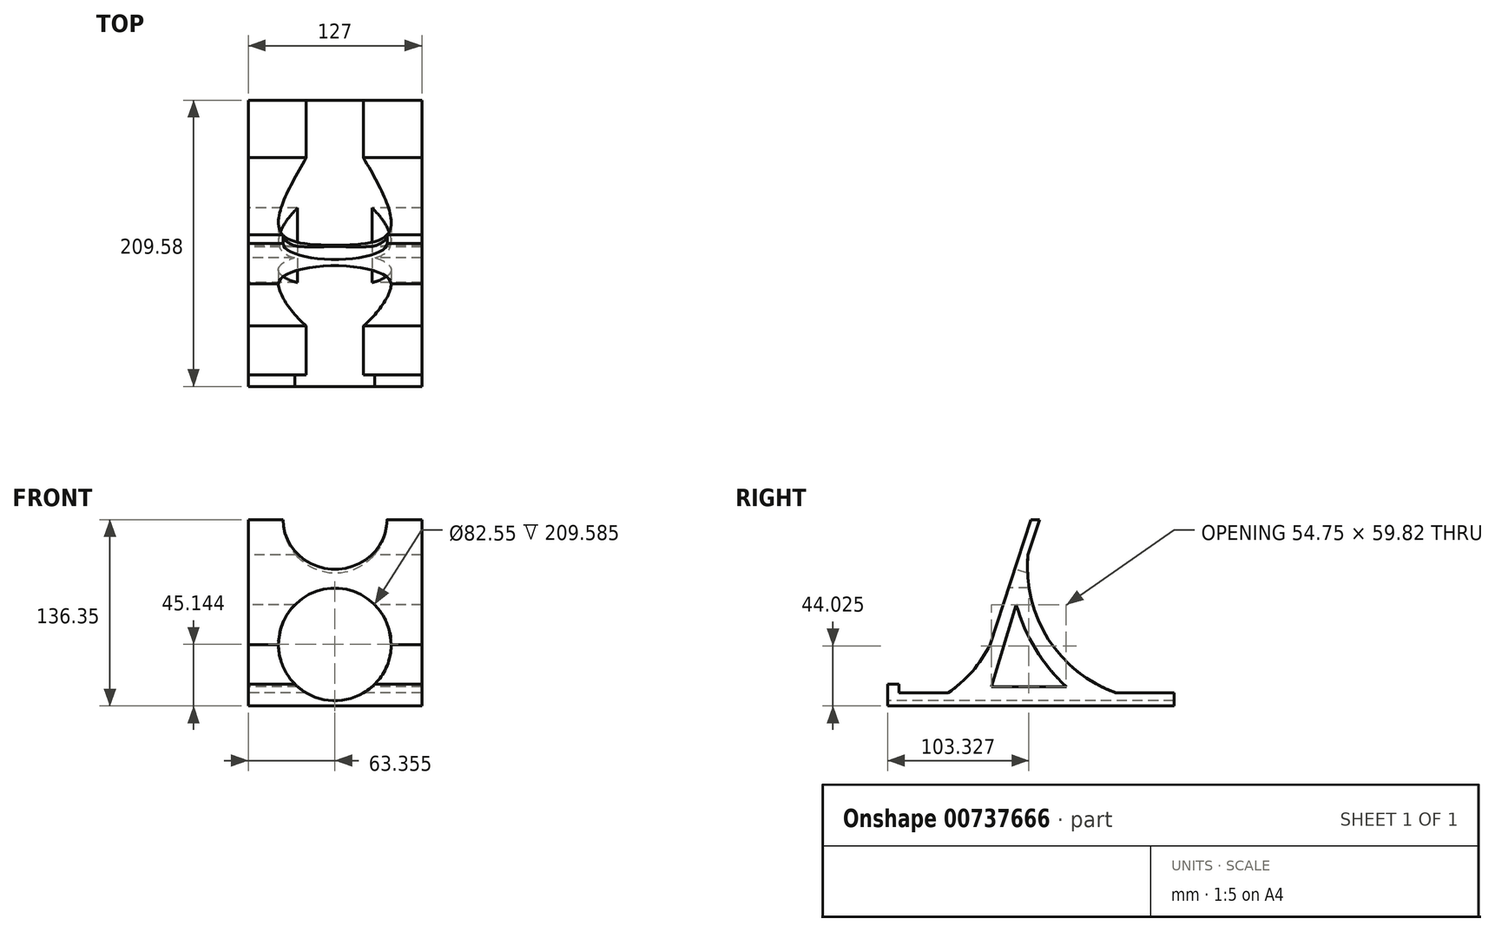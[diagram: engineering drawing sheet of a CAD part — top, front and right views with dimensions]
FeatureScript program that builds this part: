
annotation { "Feature Type Name" : "Feature", "Feature Type Description" : "" }
export const myFeature = defineFeature(function(context is Context, id is Id, definition is map)
    precondition{}
    {
        {
            var Q0;
            Q0=qCreatedBy(makeId("Right.planeOp"),FACE);
            var sketch = newSketch(context, id + "F0", { "sketchPlane" : qUnion([Q0])});
            skLineSegment(sketch, "E0", {"start": v(-80.73, -62.55) * mm, "end": v(122.47, -62.55) * mm});
            skLineSegment(sketch, "E1", {"start": v(122.47, -53.02) * mm, "end": v(122.47, -62.55) * mm});
            skLineSegment(sketch, "E2", {"start": v(-80.73, -62.55) * mm, "end": v(-80.73, -53.02) * mm});
            skLineSegment(sketch, "E3", {"start": v(-80.73, -53.02) * mm, "end": v(122.47, -53.02) * mm});
            skLineSegment(sketch, "E4", {"start": v(-80.73, -53.02) * mm, "end": v(-23.58, -53.02) * mm});
            skLineSegment(sketch, "E5", {"start": v(-23.58, -53.02) * mm, "end": v(17.63, 73.8) * mm});
            skLineSegment(sketch, "E6", {"start": v(-23.58, -53.02) * mm, "end": v(-17.23, -53.02) * mm});
            skLineSegment(sketch, "E7", {"start": v(-17.23, -53.02) * mm, "end": v(23.98, 73.8) * mm});
            skLineSegment(sketch, "E8", {"start": v(23.98, 73.8) * mm, "end": v(17.63, 73.8) * mm});
            skArc(sketch, "E9", {"start": v(15.56, 47.89) * mm, "mid": v(30.52, -13.75) * mm, "end": v(80.33, -53.02) * mm});
            skArc(sketch, "E10", {"start": v(7.1, 11.39) * mm, "mid": v(21.23, -21.03) * mm, "end": v(43.6, -48.44) * mm});
            skLineSegment(sketch, "E11", {"start": v(7.1, 11.39) * mm, "end": v(-11.16, -48.44) * mm});
            skLineSegment(sketch, "E12", {"start": v(-11.16, -48.44) * mm, "end": v(43.6, -48.44) * mm});
            skArc(sketch, "E13", {"start": v(-42.91, -53.02) * mm, "mid": v(-25.27, -37.33) * mm, "end": v(-12.1, -17.72) * mm});
            skLineSegment(sketch, "E14", {"start": v(-78.71, -53.02) * mm, "end": v(-78.71, -46.67) * mm});
            skLineSegment(sketch, "E15", {"start": v(-78.71, -46.67) * mm, "end": v(-87.11, -46.67) * mm});
            skLineSegment(sketch, "E16", {"start": v(-87.11, -46.67) * mm, "end": v(-87.11, -62.55) * mm});
            skLineSegment(sketch, "E17", {"start": v(-87.11, -62.55) * mm, "end": v(-80.73, -62.55) * mm});
            skSolve(sketch);
        }
        {
            var Q0;
            Q0=makeQuery(id+"F0.imprint","IMPRINT",FACE,{"disambiguationData":[TD([[makeQuery(id+"F0.imprint","IMPRINT",EDGE,{"derivedFrom":sQuery(id+"F0.wireOp",EDGE,"E5")}),-1.0]])]});
            var Q1;
            Q1=makeQuery(id+"F0.imprint","IMPRINT",FACE,{"disambiguationData":[TD([[makeQuery(id+"F0.imprint","IMPRINT",EDGE,{"derivedFrom":sQuery(id+"F0.wireOp",EDGE,"E0")}),1.0]])]});
            extrude(context, id + "F1", {"entities" : qUnion([Q0, Q1]), "depth" : 127 * mm, "offsetDistance" : 25.4 * mm});
        }
        {
            var Q0;
            {var subQ3=sQuery(id+"F0.wireOp",EDGE,"E9");Q0=makeQuery(id+"F0.imprint","IMPRINT",FACE,{"disambiguationData":[TD([[makeQuery(id+"F0.imprint","IMPRINT",EDGE,{"derivedFrom":subQ3}),-1.0]])]});}
            extrude(context, id + "F2", {"entities" : qUnion([Q0]), "operationType" : NewBodyOperationType.ADD, "depth" : 127 * mm, "offsetDistance" : 25.4 * mm});
        }
        {
            var Q0;
            Q0=makeQuery(id+"F0.imprint","IMPRINT",FACE,{"disambiguationData":[TD([[makeQuery(id+"F0.imprint","IMPRINT",EDGE,{"derivedFrom":sQuery(id+"F0.wireOp",EDGE,"E10")}),-1.0]])]});
            extrude(context, id + "F3", {"entities" : qUnion([Q0]), "operationType" : NewBodyOperationType.REMOVE, "oppositeDirection" : true, "depth" : 127 * mm, "offsetDistance" : 25.4 * mm});
        }
        {
            var Q0;
            {var subQ3=sQuery(id+"F0.wireOp",EDGE,"E13");Q0=makeQuery(id+"F0.imprint","IMPRINT",FACE,{"disambiguationData":[TD([[makeQuery(id+"F0.imprint","IMPRINT",EDGE,{"derivedFrom":subQ3}),-1.0]])]});}
            extrude(context, id + "F4", {"entities" : qUnion([Q0]), "operationType" : NewBodyOperationType.ADD, "depth" : 127 * mm, "offsetDistance" : 25.4 * mm});
        }
        {
            var Q0;
            {var subQ2=sQuery(id+"F0.wireOp",EDGE,"E2");Q0=makeQuery(id+"F0.imprint","IMPRINT",FACE,{"disambiguationData":[TD([[makeQuery(id+"F0.imprint","IMPRINT",EDGE,{"derivedFrom":subQ2}),1.0]])]});}
            extrude(context, id + "F5", {"entities" : qUnion([Q0]), "operationType" : NewBodyOperationType.ADD, "depth" : 127 * mm, "offsetDistance" : 25.4 * mm});
        }
        {
            var Q0;
            Q0=makeQuery(id+"F1.opExtrude","SWEPT_FACE",FACE,{"disambiguationData":[OSD([sQuery(id+"F0.wireOp",EDGE,"E5")])]});
            var sketch = newSketch(context, id + "F6", { "sketchPlane" : qUnion([Q0])});
            skCircle(sketch, "E18", {"center": v(63.5, 75.64) * mm, "radius": 38.1 * mm});
            skSolve(sketch);
        }
        {
            var Q0;
            {var subQ0=sQuery(id+"F6.wireOp",EDGE,"E18");var subQ1=makeQuery(id+"F1.opExtrude","SWEPT_EDGE",EDGE,{"disambiguationData":[OSD([sQuery(id+"F0.wireOp",EDGE,"E5"),sQuery(id+"F0.wireOp",EDGE,"E8")])]});var subQ2=makeQuery(id+"F6.imprint","INTERSECT",VERTEX,{"disambiguationData":[OD(0.0)],"derivedFrom":[subQ1,subQ0]});Q0=makeQuery(id+"F6.imprint","IMPRINT",FACE,{"disambiguationData":[TD([[makeQuery(id+"F6.imprint","IMPRINT",EDGE,{"disambiguationData":[TD([[subQ2,1.0]])],"derivedFrom":subQ0}),1.0]])]});}
            var Q1;
            {var subQ0=sQuery(id+"F6.wireOp",EDGE,"E18");var subQ1=makeQuery(id+"F1.opExtrude","SWEPT_EDGE",EDGE,{"disambiguationData":[OSD([sQuery(id+"F0.wireOp",EDGE,"E5"),sQuery(id+"F0.wireOp",EDGE,"E8")])]});var subQ2=makeQuery(id+"F6.imprint","INTERSECT",VERTEX,{"disambiguationData":[OD(0.0)],"derivedFrom":[subQ1,subQ0]});Q1=makeQuery(id+"F6.imprint","IMPRINT",FACE,{"disambiguationData":[TD([[makeQuery(id+"F6.imprint","IMPRINT",EDGE,{"disambiguationData":[TD([[subQ2,-1.0]])],"derivedFrom":subQ0}),1.0]])]});}
            var Q2;
            {var subQ0=sQuery(id+"F6.wireOp",EDGE,"gt9Bg4EX-yINn-S15B-Bd02-J4mhynKTRT1z");var subQ1=makeQuery(id+"F4.opExtrude","SWEPT_EDGE",EDGE,{"disambiguationData":[OSD([sQuery(id+"F0.wireOp",EDGE,"E5"),sQuery(id+"F0.wireOp",EDGE,"E13")])]});var subQ2=makeQuery(id+"F6.imprint","INTERSECT",VERTEX,{"disambiguationData":[OD(0.0)],"derivedFrom":[subQ1,subQ0]});Q2=makeQuery(id+"F6.imprint","IMPRINT",FACE,{"disambiguationData":[TD([[makeQuery(id+"F6.imprint","IMPRINT",EDGE,{"disambiguationData":[TD([[subQ2,-1.0]])],"derivedFrom":subQ0}),1.0]])]});}
            var Q3;
            {var subQ0=sQuery(id+"F6.wireOp",EDGE,"gt9Bg4EX-yINn-S15B-Bd02-J4mhynKTRT1z");var subQ1=makeQuery(id+"F4.opExtrude","SWEPT_EDGE",EDGE,{"disambiguationData":[OSD([sQuery(id+"F0.wireOp",EDGE,"E5"),sQuery(id+"F0.wireOp",EDGE,"E13")])]});var subQ2=makeQuery(id+"F6.imprint","INTERSECT",VERTEX,{"disambiguationData":[OD(0.0)],"derivedFrom":[subQ1,subQ0]});Q3=makeQuery(id+"F6.imprint","IMPRINT",FACE,{"disambiguationData":[TD([[makeQuery(id+"F6.imprint","IMPRINT",EDGE,{"disambiguationData":[TD([[subQ2,1.0]])],"derivedFrom":subQ0}),1.0]])]});}
            var Q4;
            Q4=sQuery(id+"F6.wireOp",EDGE,"E18");
            var Q5;
            Q5=sQuery(id+"F6.wireOp",EDGE,"gt9Bg4EX-yINn-S15B-Bd02-J4mhynKTRT1z");
            extrude(context, id + "F7", {"entities" : qUnion([Q0, Q1, Q2, Q3]), "operationType" : NewBodyOperationType.REMOVE, "surfaceEntities" : qUnion([Q4, Q5]), "oppositeDirection" : true, "depth" : 114.3 * mm, "offsetDistance" : 25.4 * mm});
        }
        {
            var Q0;
            Q0=makeQuery(id+"F5.opExtrude","SWEPT_FACE",FACE,{"disambiguationData":[OSD([sQuery(id+"F0.wireOp",EDGE,"E16")])]});
            var sketch = newSketch(context, id + "F8", { "sketchPlane" : qUnion([Q0])});
            skCircle(sketch, "E19", {"center": v(63.35, -17.4) * mm, "radius": 41.28 * mm});
            skSolve(sketch);
        }
        {
            var Q0;
            {var subQ0=sQuery(id+"F8.wireOp",EDGE,"E19");var subQ1=makeQuery(id+"F5.opExtrude","SWEPT_EDGE",EDGE,{"disambiguationData":[OSD([sQuery(id+"F0.wireOp",EDGE,"E15"),sQuery(id+"F0.wireOp",EDGE,"E16")])]});var subQ2=makeQuery(id+"F8.imprint","INTERSECT",VERTEX,{"disambiguationData":[OD(0.0)],"derivedFrom":[subQ1,subQ0]});Q0=makeQuery(id+"F8.imprint","IMPRINT",FACE,{"disambiguationData":[TD([[makeQuery(id+"F8.imprint","IMPRINT",EDGE,{"disambiguationData":[TD([[subQ2,1.0]])],"derivedFrom":subQ0}),1.0]])]});}
            var Q1;
            {var subQ0=sQuery(id+"F8.wireOp",EDGE,"E19");var subQ1=makeQuery(id+"F5.opExtrude","SWEPT_EDGE",EDGE,{"disambiguationData":[OSD([sQuery(id+"F0.wireOp",EDGE,"E15"),sQuery(id+"F0.wireOp",EDGE,"E16")])]});var subQ2=makeQuery(id+"F8.imprint","INTERSECT",VERTEX,{"disambiguationData":[OD(0.0)],"derivedFrom":[subQ1,subQ0]});Q1=makeQuery(id+"F8.imprint","IMPRINT",FACE,{"disambiguationData":[TD([[makeQuery(id+"F8.imprint","IMPRINT",EDGE,{"disambiguationData":[TD([[subQ2,-1.0]])],"derivedFrom":subQ0}),1.0]])]});}
            var Q2;
            Q2=sQuery(id+"F8.wireOp",EDGE,"E19");
            extrude(context, id + "F9", {"entities" : qUnion([Q0, Q1]), "operationType" : NewBodyOperationType.REMOVE, "surfaceEntities" : qUnion([Q2]), "oppositeDirection" : true, "depth" : 215.9 * mm, "offsetDistance" : 25.4 * mm});
        }
    });
